# Revit family: 3-547-xx-BPxx - 37-547-xx-BPxx - Balance (Vanity)
name_source: partatom
category: Lighting Fixtures
revit_build: Autodesk Revit 2018 (Build: 20180423_1000(x64)
units: mm (PartAtom-declared; Revit-internal decimal feet)

## family parameters
Cut with Voids When Loaded = No
Host = Face
Light Source = No
Part Type = Normal
Room Calculation Point = No
Round Connector Dimension = Use Diameter
Shared = No

## types (4) — shared parameters
Diffuser = Matte White Acrylic
Lamp = LED Array
Manufacturer = Oxygen Lighting
Model = 3-547-xx-BPxx / 37-547-xx-BPxx - Balance
Other = <By Category>
URL = www.oxygenlighting.com
Wattage Comments = 14.5 W at 120 V
zero-valued in all types: Default Elevation

## per-type parameters (varying)
| type | Fixture | Metal Finish |
| 3-547-20 / 37-547-20 - Balance | 3-547 Balance | 20 - Polished Nickel |
| 3-547-20-BP20 / 37-547-20-BP20 - Balance | 3-547 Balance BP | 20 - Polished Nickel |
| 3-547-24-BP24 / 37-547-24-BP24 - Balance | 3-547 Balance BP | 24 - Satin Nickel |
| 3-547-24 / 37-547-24 - Balance | 3-547 Balance | 24 - Satin Nickel |

## geometry (parser evidence)
native form markers: Sweep x11
no freeform markers — native parametric forms only
